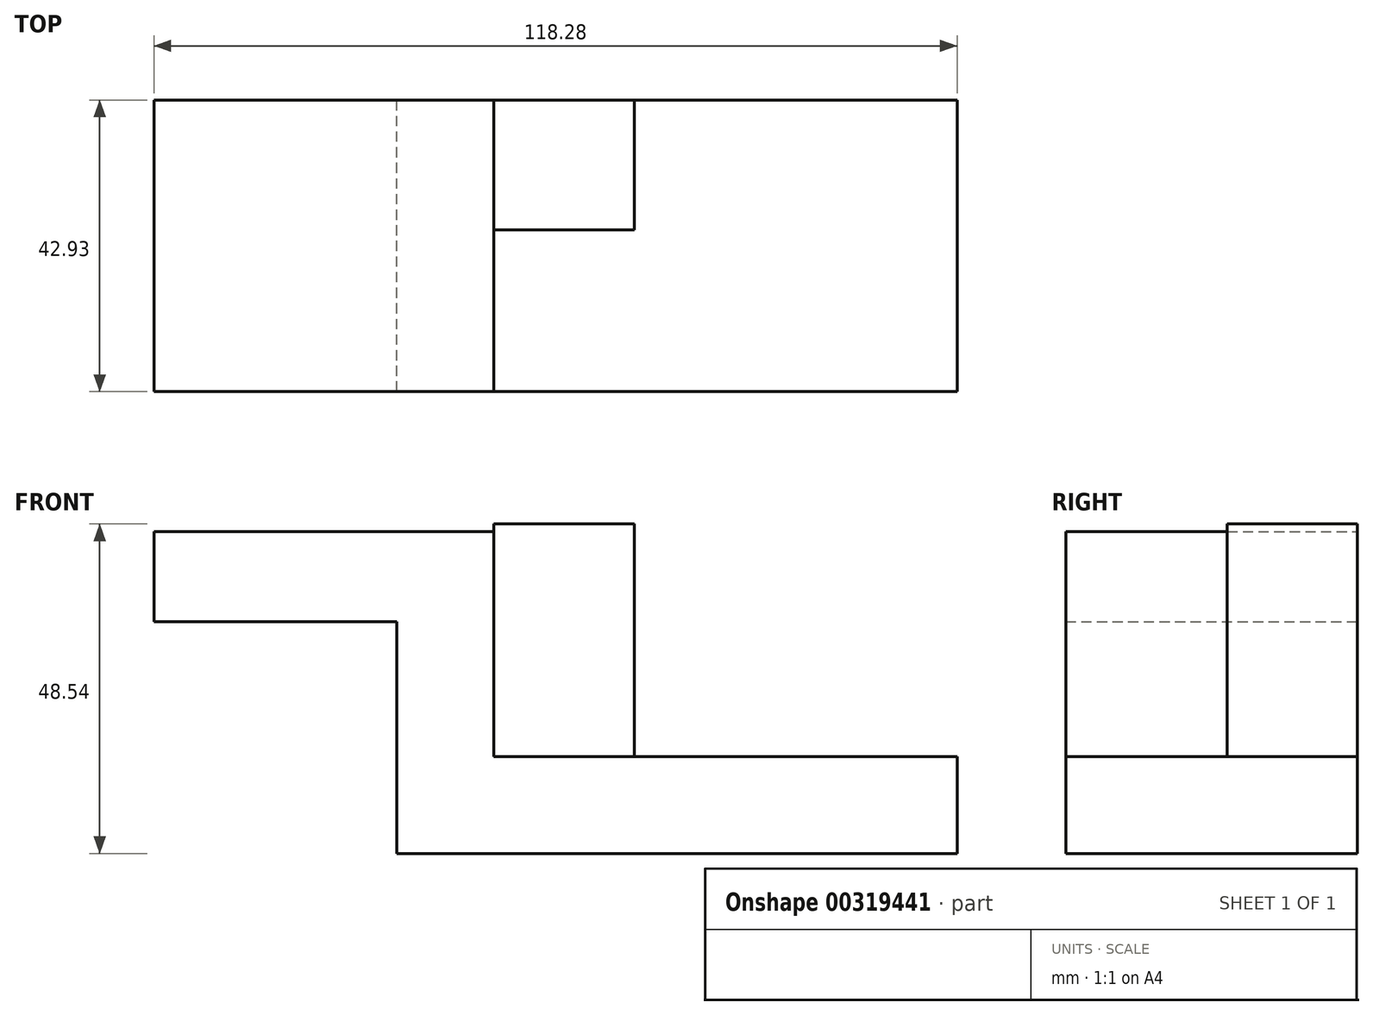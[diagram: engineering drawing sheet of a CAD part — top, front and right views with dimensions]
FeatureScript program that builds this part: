
annotation { "Feature Type Name" : "Feature", "Feature Type Description" : "" }
export const myFeature = defineFeature(function(context is Context, id is Id, definition is map)
    precondition{}
    {
        {
            var Q0;
            Q0=qCreatedBy(makeId("Front.planeOp"),FACE);
            var sketch = newSketch(context, id + "F0", { "sketchPlane" : qUnion([Q0])});
            skLineSegment(sketch, "E0", {"start": v(59.8, -47.38) * mm, "end": v(-22.7, -47.38) * mm});
            skLineSegment(sketch, "E1", {"start": v(-22.7, -47.38) * mm, "end": v(-22.7, -13.25) * mm});
            skLineSegment(sketch, "E2", {"start": v(-22.7, -13.25) * mm, "end": v(-58.48, -13.25) * mm});
            skLineSegment(sketch, "E3", {"start": v(-58.48, -13.25) * mm, "end": v(-58.48, 0) * mm});
            skLineSegment(sketch, "E4", {"start": v(-58.48, 0) * mm, "end": v(-8.45, 0) * mm});
            skLineSegment(sketch, "E5", {"start": v(-8.45, 0) * mm, "end": v(-8.45, -33.13) * mm});
            skLineSegment(sketch, "E6", {"start": v(-8.45, -33.13) * mm, "end": v(59.8, -33.13) * mm});
            skLineSegment(sketch, "E7", {"start": v(59.8, -33.13) * mm, "end": v(59.8, -47.38) * mm});
            skSolve(sketch);
        }
        {
            var Q0;
            Q0 = qSketchRegion(id + "F0", true);
            extrude(context, id + "F1", {"entities" : qUnion([Q0]), "depth" : 42.93 * mm});
        }
        {
            var Q0;
            Q0=makeQuery(id+"F1.opExtrude","SWEPT_FACE",FACE,{"disambiguationData":[OSD([sQuery(id+"F0.wireOp",EDGE,"E6")])]});
            var sketch = newSketch(context, id + "F2", { "sketchPlane" : qUnion([Q0])});
            skLineSegment(sketch, "E8", {"start": v(-8.45, -19.13) * mm, "end": v(12.28, -19.13) * mm});
            skLineSegment(sketch, "E9", {"start": v(12.28, -19.13) * mm, "end": v(12.28, 0) * mm});
            skLineSegment(sketch, "E10", {"start": v(12.28, 0) * mm, "end": v(-8.45, 0) * mm});
            skLineSegment(sketch, "E11", {"start": v(-8.45, 0) * mm, "end": v(-8.45, -19.13) * mm});
            skSolve(sketch);
        }
        {
            var Q0;
            Q0=makeQuery(id+"F2.imprint","IMPRINT",FACE,{"disambiguationData":[TD([[makeQuery(id+"F2.imprint","IMPRINT",EDGE,{"derivedFrom":sQuery(id+"F2.wireOp",EDGE,"E8")}),1.0]])]});
            extrude(context, id + "F3", {"entities" : qUnion([Q0]), "operationType" : NewBodyOperationType.ADD, "depth" : 34.3 * mm});
        }
    });
